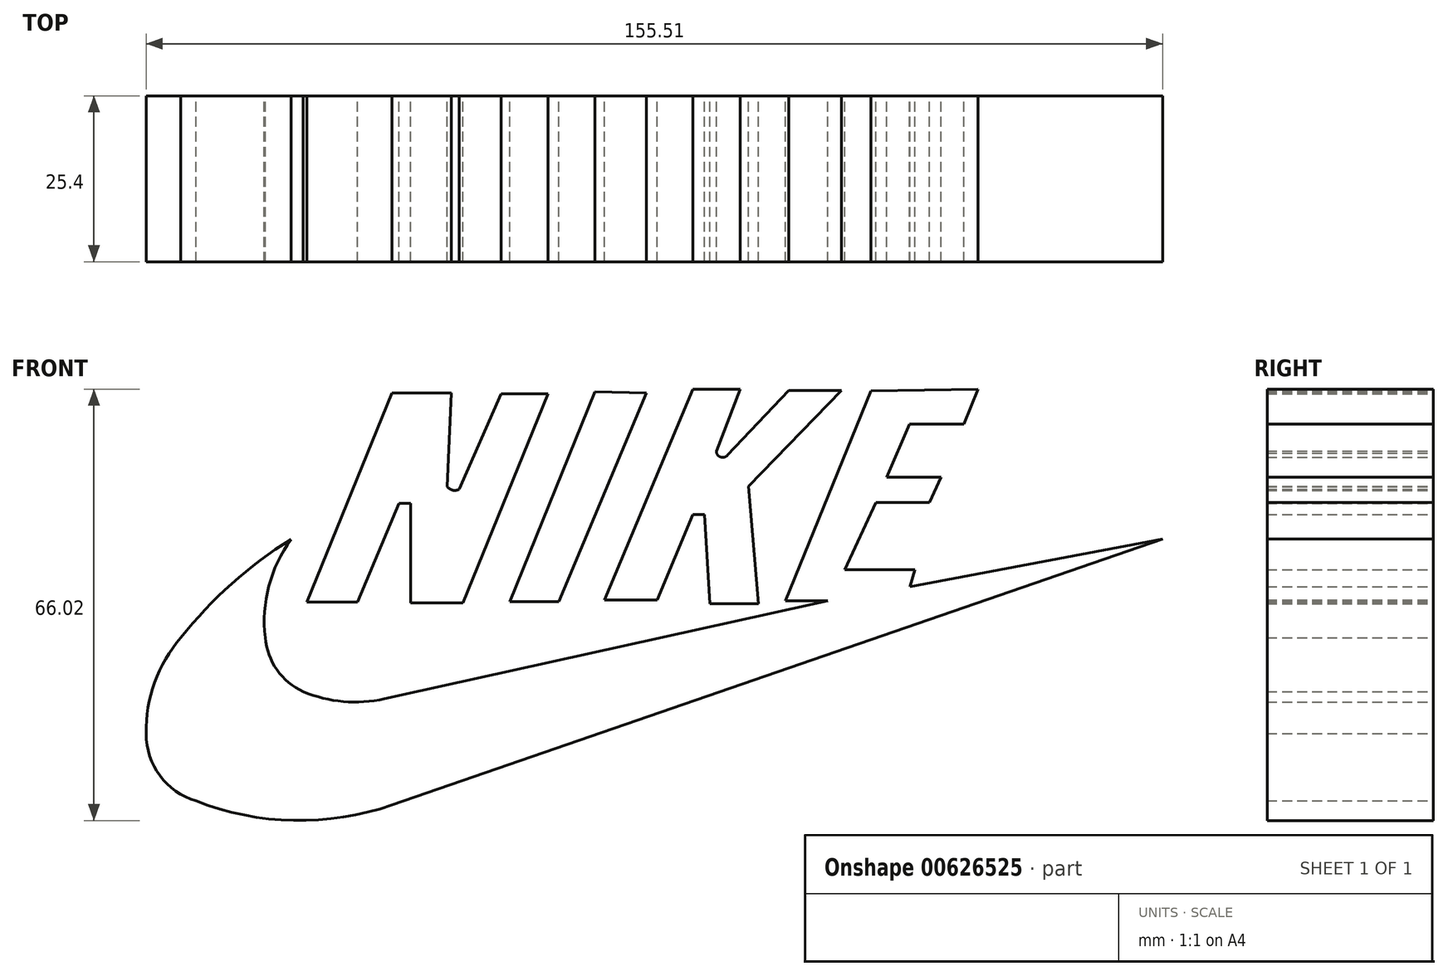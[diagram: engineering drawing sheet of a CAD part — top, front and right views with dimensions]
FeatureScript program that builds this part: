
annotation { "Feature Type Name" : "Feature", "Feature Type Description" : "" }
export const myFeature = defineFeature(function(context is Context, id is Id, definition is map)
    precondition{}
    {
        {
            var Q0;
            Q0=qCreatedBy(makeId("Front.planeOp"),FACE);
            var sketch = newSketch(context, id + "F0", { "sketchPlane" : qUnion([Q0])});
            skLineSegment(sketch, "E0", {"start": v(-46.6, 28.26) * mm, "end": v(-33.55, 60.3) * mm});
            skLineSegment(sketch, "E1", {"start": v(-33.55, 60.3) * mm, "end": v(-24.5, 60.3) * mm});
            skLineSegment(sketch, "E2", {"start": v(-46.6, 28.26) * mm, "end": v(-38.8, 28.26) * mm});
            skLineSegment(sketch, "E3", {"start": v(-38.8, 28.26) * mm, "end": v(-32.48, 43.36) * mm});
            skLineSegment(sketch, "E4", {"start": v(-32.48, 43.36) * mm, "end": v(-30.69, 43.36) * mm});
            skLineSegment(sketch, "E5", {"start": v(-30.69, 43.36) * mm, "end": v(-30.69, 28.16) * mm});
            skLineSegment(sketch, "E6", {"start": v(-30.69, 28.16) * mm, "end": v(-22.7, 28.16) * mm});
            skLineSegment(sketch, "E7", {"start": v(-22.7, 28.16) * mm, "end": v(-9.67, 60.16) * mm});
            skLineSegment(sketch, "E8", {"start": v(-9.67, 60.16) * mm, "end": v(-16.86, 60.16) * mm});
            skLineSegment(sketch, "E9", {"start": v(-16.86, 60.16) * mm, "end": v(-23.29, 45.53) * mm});
            skLineSegment(sketch, "E10", {"start": v(-24.5, 60.3) * mm, "end": v(-25.1, 45.92) * mm});
            skArc(sketch, "E11", {"start": v(-25.1, 45.92) * mm, "mid": v(-24.26, 45.39) * mm, "end": v(-23.29, 45.53) * mm});
            skLineSegment(sketch, "E12", {"start": v(-2.54, 60.46) * mm, "end": v(-15.54, 28.33) * mm});
            skLineSegment(sketch, "E13", {"start": v(-15.54, 28.33) * mm, "end": v(-8.02, 28.33) * mm});
            skLineSegment(sketch, "E14", {"start": v(-8.02, 28.33) * mm, "end": v(5.39, 60.3) * mm});
            skLineSegment(sketch, "E15", {"start": v(5.39, 60.3) * mm, "end": v(-2.54, 60.46) * mm});
            skLineSegment(sketch, "E16", {"start": v(39.7, 60.58) * mm, "end": v(26.66, 28.45) * mm});
            skLineSegment(sketch, "E17", {"start": v(26.66, 28.45) * mm, "end": v(33.08, 28.45) * mm});
            skLineSegment(sketch, "E18", {"start": v(33.08, 28.45) * mm, "end": v(45.67, 30.6) * mm});
            skLineSegment(sketch, "E19", {"start": v(45.67, 30.6) * mm, "end": v(46.47, 33.2) * mm});
            skLineSegment(sketch, "E20", {"start": v(46.47, 33.2) * mm, "end": v(35.7, 33.2) * mm});
            skLineSegment(sketch, "E21", {"start": v(35.7, 33.2) * mm, "end": v(40.45, 43.51) * mm});
            skLineSegment(sketch, "E22", {"start": v(40.45, 43.51) * mm, "end": v(48.68, 43.51) * mm});
            skLineSegment(sketch, "E23", {"start": v(48.68, 43.51) * mm, "end": v(50.42, 47.4) * mm});
            skLineSegment(sketch, "E24", {"start": v(50.42, 47.4) * mm, "end": v(42.12, 47.4) * mm});
            skLineSegment(sketch, "E25", {"start": v(42.12, 47.4) * mm, "end": v(45.6, 55.5) * mm});
            skLineSegment(sketch, "E26", {"start": v(45.6, 55.5) * mm, "end": v(53.97, 55.5) * mm});
            skLineSegment(sketch, "E27", {"start": v(53.97, 55.5) * mm, "end": v(56.11, 60.85) * mm});
            skLineSegment(sketch, "E28", {"start": v(56.11, 60.85) * mm, "end": v(39.7, 60.58) * mm});
            skLineSegment(sketch, "E29", {"start": v(12.5, 60.84) * mm, "end": v(19.72, 60.84) * mm});
            skLineSegment(sketch, "E30", {"start": v(19.72, 60.84) * mm, "end": v(16.11, 51.35) * mm});
            skLineSegment(sketch, "E31", {"start": v(12.5, 60.84) * mm, "end": v(-1.02, 28.6) * mm});
            skLineSegment(sketch, "E32", {"start": v(-1.02, 28.6) * mm, "end": v(7.04, 28.6) * mm});
            skLineSegment(sketch, "E33", {"start": v(7.04, 28.6) * mm, "end": v(12.5, 41.64) * mm});
            skLineSegment(sketch, "E34", {"start": v(12.5, 41.64) * mm, "end": v(14.26, 41.64) * mm});
            skLineSegment(sketch, "E35", {"start": v(14.26, 41.64) * mm, "end": v(15.08, 28.04) * mm});
            skLineSegment(sketch, "E36", {"start": v(15.08, 28.04) * mm, "end": v(22.5, 28.04) * mm});
            skLineSegment(sketch, "E37", {"start": v(22.5, 28.04) * mm, "end": v(20.96, 45.99) * mm});
            skLineSegment(sketch, "E38", {"start": v(20.96, 45.99) * mm, "end": v(35.2, 60.64) * mm});
            skLineSegment(sketch, "E39", {"start": v(35.2, 60.64) * mm, "end": v(27.15, 60.64) * mm});
            skLineSegment(sketch, "E40", {"start": v(27.15, 60.64) * mm, "end": v(17.76, 50.73) * mm});
            skArc(sketch, "E41", {"start": v(16.11, 51.04) * mm, "mid": v(16.85, 50.44) * mm, "end": v(17.76, 50.73) * mm});
            skLineSegment(sketch, "E42", {"start": v(16.11, 51.35) * mm, "end": v(16.11, 51.04) * mm});
            skLineSegment(sketch, "E43", {"start": v(84.34, 37.92) * mm, "end": v(-33.56, -2.8) * mm});
            skLineSegment(sketch, "E44", {"start": v(84.34, 37.92) * mm, "end": v(45.67, 30.6) * mm});
            skLineSegment(sketch, "E45", {"start": v(33.08, 28.45) * mm, "end": v(-34.7, 13.46) * mm});
            skArc(sketch, "E46", {"start": v(-47.14, 14.54) * mm, "mid": v(-41, 13.04) * mm, "end": v(-34.7, 13.46) * mm});
            skArc(sketch, "E47", {"start": v(-52.95, 22.8) * mm, "mid": v(-51.15, 17.9) * mm, "end": v(-47.14, 14.54) * mm});
            skArc(sketch, "E48", {"start": v(-48.99, 37.85) * mm, "mid": v(-52.4, 30.7) * mm, "end": v(-52.95, 22.8) * mm});
            skArc(sketch, "E49", {"start": v(-48.99, 37.85) * mm, "mid": v(-58.09, 31.07) * mm, "end": v(-65.86, 22.8) * mm});
            skArc(sketch, "E50", {"start": v(-65.86, 22.8) * mm, "mid": v(-69.88, 15.96) * mm, "end": v(-71.16, 8.13) * mm});
            skArc(sketch, "E51", {"start": v(-71.16, 8.13) * mm, "mid": v(-69.07, 1.7) * mm, "end": v(-63.55, -2.17) * mm});
            skArc(sketch, "E52", {"start": v(-63.55, -2.17) * mm, "mid": v(-48.6, -5.16) * mm, "end": v(-33.56, -2.8) * mm});
            skSolve(sketch);
        }
        {
            var Q0;
            Q0=makeQuery(id+"F0.imprint","IMPRINT",FACE,{"disambiguationData":[TD([[makeQuery(id+"F0.imprint","IMPRINT",EDGE,{"derivedFrom":sQuery(id+"F0.wireOp",EDGE,"E0")}),-1.0]])]});
            var Q1;
            Q1=makeQuery(id+"F0.imprint","IMPRINT",FACE,{"disambiguationData":[TD([[makeQuery(id+"F0.imprint","IMPRINT",EDGE,{"derivedFrom":sQuery(id+"F0.wireOp",EDGE,"E12")}),1.0]])]});
            var Q2;
            Q2=makeQuery(id+"F0.imprint","IMPRINT",FACE,{"disambiguationData":[TD([[makeQuery(id+"F0.imprint","IMPRINT",EDGE,{"derivedFrom":sQuery(id+"F0.wireOp",EDGE,"E29")}),-1.0]])]});
            var Q3;
            Q3=makeQuery(id+"F0.imprint","IMPRINT",FACE,{"disambiguationData":[TD([[makeQuery(id+"F0.imprint","IMPRINT",EDGE,{"derivedFrom":sQuery(id+"F0.wireOp",EDGE,"E16")}),1.0]])]});
            var Q4;
            Q4=makeQuery(id+"F0.imprint","IMPRINT",FACE,{"disambiguationData":[TD([[makeQuery(id+"F0.imprint","IMPRINT",EDGE,{"derivedFrom":sQuery(id+"F0.wireOp",EDGE,"E18")}),-1.0]])]});
            extrude(context, id + "F1", {"entities" : qUnion([Q0, Q1, Q2, Q3, Q4]), "depth" : 25.4 * mm, "offsetDistance" : 25.4 * mm});
        }
    });
